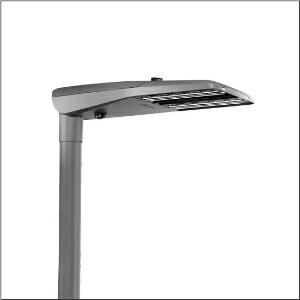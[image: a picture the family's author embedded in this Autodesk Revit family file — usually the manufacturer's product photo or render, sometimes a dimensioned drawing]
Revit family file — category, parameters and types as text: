
# Revit family: streetlight_sl_11_iq_midi___st1_2a_5xc3a41y08le_52ec
name_source: partatom
category: Lighting Fixtures
units: mm (PartAtom-declared; Revit-internal decimal feet)

## family parameters
Cut with Voids When Loaded = No
Host = Face
Light Source = No
Part Type = Normal
Room Calculation Point = No
Round Connector Dimension = Use Diameter
Shared = No

## types (1)
- --- (1 x LED, 9590 lm, 59.4 W, 4000K)
    Apparent Load = 59 VA
    CIE Flux Codes = 32 70 96 100 100
    Color Rendering = 70
    Color Temperature = 4000K
    Default Elevation = 1800 mm
    Description = Streetlight SL 11 iQ midi, mast luminaire, primary light control with 3 zone facetted reflector, of plastic, silver coated, highly specular, primary optical cover: cover, of PMMA, transparent, light distribution: ST1.2a, light emission: direct distribution, primary light characteristic: asymmetric, installation type: post-top, side-entry, LED, High Power LED, rated luminous flux: 9.590lm, luminous efficacy: 161lm/W, light colour: 740, colour temperature: 4000K, control: presetting dimming logarithmic, Street-Remote, Auto-Match, Temp-Guard, Lumen-Switch, Night-Set, Smart-Wire, Light-Fading, Desk-Remote (wireless, voltage-free reading and setting of iQ features in the workshop via application-optimized NFC function/RFID function), optimised constant luminous flux control (CLO 2.0), with cable H07RN-F 5x 1.5mm², mains connection: 230..240V, AC, 50/60Hz, connection cable pre-assembled, cable length: 8,5m, start of lifetime: 59W, end of service life: 62W, reduction: 29W, luminaire housing, of diecast aluminium, powder-coated, Siteco® metallic grey (DB 702S), please order mast flange separately, inclination adjustable without tools: 0°, 5°, 10°, 15° (post-top) | 0°, -5°, -10°, -15° (side-entry), sealing non-destructively replaceable, multi-level sealing system, length: 780mm, width: 376mm, height: 118mm, mast flange for spigot size: 42mm (side-entry): 5XC10008XM4, 60/48mm (side-entry/post-top): 5XC10108XM2, 76/60mm (side-entry/post-top): 5XC10108XM1, equipment: standard, Smart Interface below and above, protection rating (complete): IP66, insulation class (complete): insulation class II (safety insulation), certification: CE, ENEC, VDE, UKCA, impact resistance: IK09, permissible operating ambient temperature for outdoor applications: -25..+50°C, standard-compliant lighting for roads and squares, Environmental Product Declaration (EPD) tested and certified by an independent institute, packaging unit: 1 piece

Light Distribution: ST1.2a
    Height = 118 mm
    Lamp = 1 x LED
    Lamp Light Flux = 9590 lm
    Lamp Power = 59.4 W
    Lamp count = 1
    Length = 780 mm
    Luminous efficacy = 161 lm/W
    Manufacturer = Siteco
    ModVariant = No
    Model = 5XC3A41Y08LE
    Number of Poles = 1
    OnlyDefault = Yes
    Power Factor = 1
    Product Name = Streetlight SL 11 iQ midi | ST1.2a
    Product group = mast luminaire | pylon top
    ProductGroupID = 6100
    Protection Class = Protection class II
    Protection Degree = IP 66
    RLX_Detail_Level = 1
    RLX_Emergency_Light_Flux = 0 lm
    RLX_Emergency_Type = 0
    RLX_Emergency_Type_DB = No
    RlxData = <blob elided: 69697 chars, md5=ca3e9554>
    Socket = socket
    Standby Power = 0 W
    System Light Flux = 9590 lm
    System Power = 59 W
    Type Comments = factory setting: luminous flux: 100 % | dim-lin: 254 | 521 mA
    Type Image = l_1004429.jpg
    URL = http://relux.com
    VarID = @adj_064523
    Voltage = 0 V
    Weight = 0.00 kg
    Width = 376 mm

## geometry (parser evidence)
native form markers: Blend x4, Sweep x8
no freeform markers — native parametric forms only
